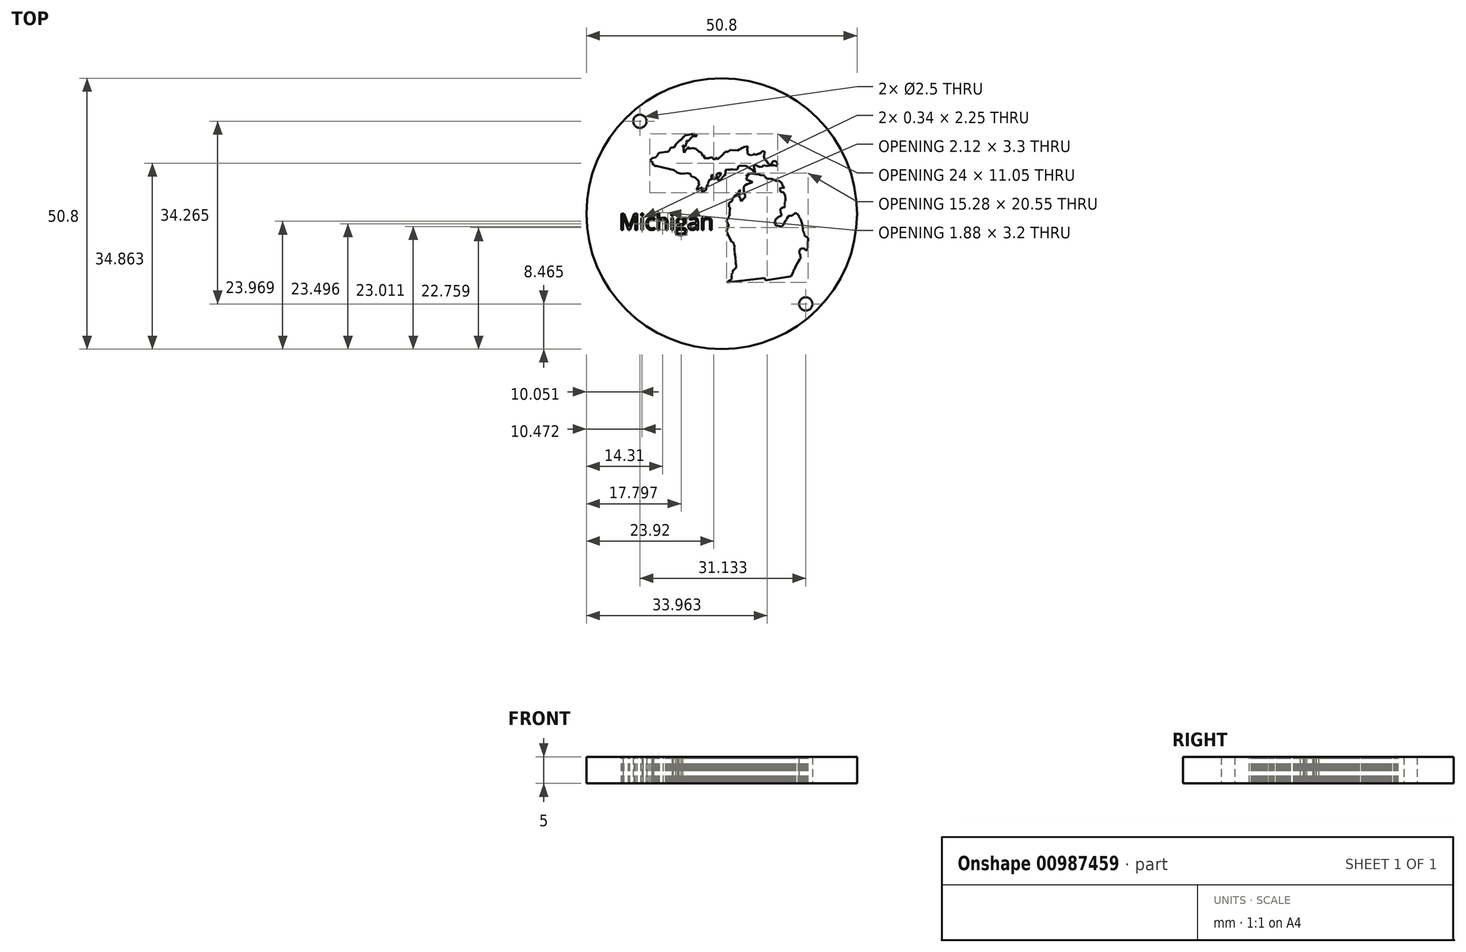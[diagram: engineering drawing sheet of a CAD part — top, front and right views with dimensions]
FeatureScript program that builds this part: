
annotation { "Feature Type Name" : "Feature", "Feature Type Description" : "" }
export const myFeature = defineFeature(function(context is Context, id is Id, definition is map)
    precondition{}
    {
        {
            var Q0;
            Q0=qCreatedBy(makeId("Top.planeOp"),FACE);
            var sketch = newSketch(context, id + "F0", { "sketchPlane" : qUnion([Q0])});
            skCircle(sketch, "E0", {"center": v(0, 0) * mm, "radius": 25.4 * mm});
            skCircle(sketch, "E1", {"center": v(-15.35, 17.33) * mm, "radius": 1.25 * mm});
            skCircle(sketch, "E2", {"center": v(15.78, -16.94) * mm, "radius": 1.25 * mm});
            skSolve(sketch);
        }
        {
            var Q0;
            Q0 = qSketchRegion(id + "F0", true);
            extrude(context, id + "F1", {"entities" : qUnion([Q0]), "depth" : 5 * mm, "offsetDistance" : 25 * mm});
        }
        {
            var Q0;
            Q0=makeQuery(id+"F1.opExtrude","CAP_FACE",FACE,{"disambiguationData":[OSD([sQuery(id+"F0.wireOp",EDGE,"E0"),sQuery(id+"F0.wireOp",EDGE,"E1"),sQuery(id+"F0.wireOp",EDGE,"E2")])],"isStart":false});
            var sketch = newSketch(context, id + "F2", { "sketchPlane" : qUnion([Q0])});
            skLineSegment(sketch, "E3", {"start": v(-7.31, 12.84) * mm, "end": v(-7.13, 12.4) * mm});
            skLineSegment(sketch, "E4", {"start": v(-7.13, 12.4) * mm, "end": v(-7.13, 11.84) * mm});
            skLineSegment(sketch, "E5", {"start": v(-7.13, 11.84) * mm, "end": v(-7.03, 11.43) * mm});
            skLineSegment(sketch, "E6", {"start": v(-7.03, 11.43) * mm, "end": v(-6.81, 11.86) * mm});
            skLineSegment(sketch, "E7", {"start": v(-6.81, 11.86) * mm, "end": v(-6.68, 12.01) * mm});
            skLineSegment(sketch, "E8", {"start": v(-6.68, 12.01) * mm, "end": v(-6.24, 12.44) * mm});
            skLineSegment(sketch, "E9", {"start": v(-6.24, 12.44) * mm, "end": v(-6.19, 12.44) * mm});
            skLineSegment(sketch, "E10", {"start": v(-6.19, 12.44) * mm, "end": v(-6.16, 12.37) * mm});
            skLineSegment(sketch, "E11", {"start": v(-6.16, 12.37) * mm, "end": v(-6.24, 12.27) * mm});
            skLineSegment(sketch, "E12", {"start": v(-6.24, 12.27) * mm, "end": v(-6.21, 12.17) * mm});
            skLineSegment(sketch, "E13", {"start": v(-6.21, 12.17) * mm, "end": v(-5.78, 12.22) * mm});
            skLineSegment(sketch, "E14", {"start": v(-5.78, 12.22) * mm, "end": v(-5.48, 12.33) * mm});
            skLineSegment(sketch, "E15", {"start": v(-5.48, 12.33) * mm, "end": v(-4.86, 12.2) * mm});
            skLineSegment(sketch, "E16", {"start": v(-4.86, 12.2) * mm, "end": v(-4.25, 11.64) * mm});
            skLineSegment(sketch, "E17", {"start": v(-4.25, 11.64) * mm, "end": v(-3.88, 11.5) * mm});
            skLineSegment(sketch, "E18", {"start": v(-3.88, 11.5) * mm, "end": v(-3.8, 11.41) * mm});
            skLineSegment(sketch, "E19", {"start": v(-3.8, 11.41) * mm, "end": v(-3.65, 11.04) * mm});
            skLineSegment(sketch, "E20", {"start": v(-3.65, 11.04) * mm, "end": v(-3.65, 10.97) * mm});
            skLineSegment(sketch, "E21", {"start": v(-3.65, 10.97) * mm, "end": v(-3.57, 10.86) * mm});
            skLineSegment(sketch, "E22", {"start": v(-3.57, 10.86) * mm, "end": v(-3.47, 10.86) * mm});
            skLineSegment(sketch, "E23", {"start": v(-3.47, 10.86) * mm, "end": v(-3.3, 10.9) * mm});
            skLineSegment(sketch, "E24", {"start": v(-3.3, 10.9) * mm, "end": v(-3.22, 10.82) * mm});
            skLineSegment(sketch, "E25", {"start": v(-3.22, 10.82) * mm, "end": v(-3.26, 10.58) * mm});
            skLineSegment(sketch, "E26", {"start": v(-3.26, 10.58) * mm, "end": v(-3.26, 10.44) * mm});
            skLineSegment(sketch, "E27", {"start": v(-3.26, 10.44) * mm, "end": v(-2.43, 10.44) * mm});
            skLineSegment(sketch, "E28", {"start": v(-2.43, 10.44) * mm, "end": v(-1.89, 10.61) * mm});
            skLineSegment(sketch, "E29", {"start": v(-1.89, 10.61) * mm, "end": v(-1.55, 10.3) * mm});
            skLineSegment(sketch, "E30", {"start": v(-1.55, 10.3) * mm, "end": v(-1.3, 10.16) * mm});
            skLineSegment(sketch, "E31", {"start": v(-1.3, 10.16) * mm, "end": v(-1.17, 10.31) * mm});
            skLineSegment(sketch, "E32", {"start": v(-1.17, 10.31) * mm, "end": v(-1.1, 10.45) * mm});
            skLineSegment(sketch, "E33", {"start": v(-1.1, 10.45) * mm, "end": v(-0.95, 10.45) * mm});
            skLineSegment(sketch, "E34", {"start": v(-0.95, 10.45) * mm, "end": v(-0.83, 10.26) * mm});
            skLineSegment(sketch, "E35", {"start": v(-0.83, 10.26) * mm, "end": v(-0.73, 10.21) * mm});
            skLineSegment(sketch, "E36", {"start": v(-0.73, 10.21) * mm, "end": v(0, 10.93) * mm});
            skLineSegment(sketch, "E37", {"start": v(0, 10.93) * mm, "end": v(0.07, 11) * mm});
            skLineSegment(sketch, "E38", {"start": v(0.07, 11) * mm, "end": v(0.15, 11.03) * mm});
            skLineSegment(sketch, "E39", {"start": v(0.15, 11.03) * mm, "end": v(0.18, 11.13) * mm});
            skLineSegment(sketch, "E40", {"start": v(0.18, 11.13) * mm, "end": v(0.34, 11.13) * mm});
            skLineSegment(sketch, "E41", {"start": v(0.34, 11.13) * mm, "end": v(0.37, 11.27) * mm});
            skLineSegment(sketch, "E42", {"start": v(0.37, 11.27) * mm, "end": v(0.71, 11.64) * mm});
            skLineSegment(sketch, "E43", {"start": v(0.71, 11.64) * mm, "end": v(1.16, 11.64) * mm});
            skLineSegment(sketch, "E44", {"start": v(1.16, 11.64) * mm, "end": v(1.6, 11.92) * mm});
            skLineSegment(sketch, "E45", {"start": v(1.6, 11.92) * mm, "end": v(1.74, 11.92) * mm});
            skLineSegment(sketch, "E46", {"start": v(1.74, 11.92) * mm, "end": v(1.8, 11.86) * mm});
            skLineSegment(sketch, "E47", {"start": v(1.8, 11.86) * mm, "end": v(1.84, 11.92) * mm});
            skLineSegment(sketch, "E48", {"start": v(1.84, 11.92) * mm, "end": v(3, 11.86) * mm});
            skLineSegment(sketch, "E49", {"start": v(3, 11.86) * mm, "end": v(3.33, 12.08) * mm});
            skLineSegment(sketch, "E50", {"start": v(3.33, 12.08) * mm, "end": v(3.46, 12.08) * mm});
            skLineSegment(sketch, "E51", {"start": v(3.46, 12.08) * mm, "end": v(3.53, 12.02) * mm});
            skLineSegment(sketch, "E52", {"start": v(3.53, 12.02) * mm, "end": v(3.58, 12.26) * mm});
            skLineSegment(sketch, "E53", {"start": v(3.58, 12.26) * mm, "end": v(3.69, 12.3) * mm});
            skLineSegment(sketch, "E54", {"start": v(3.69, 12.3) * mm, "end": v(3.77, 12.21) * mm});
            skLineSegment(sketch, "E55", {"start": v(3.77, 12.21) * mm, "end": v(3.78, 12.33) * mm});
            skLineSegment(sketch, "E56", {"start": v(3.78, 12.33) * mm, "end": v(3.9, 12.37) * mm});
            skLineSegment(sketch, "E57", {"start": v(3.9, 12.37) * mm, "end": v(4.04, 12.26) * mm});
            skLineSegment(sketch, "E58", {"start": v(4.04, 12.26) * mm, "end": v(4.05, 12.48) * mm});
            skLineSegment(sketch, "E59", {"start": v(4.05, 12.48) * mm, "end": v(4.9, 12.65) * mm});
            skLineSegment(sketch, "E60", {"start": v(4.9, 12.65) * mm, "end": v(4.79, 12.11) * mm});
            skLineSegment(sketch, "E61", {"start": v(4.79, 12.11) * mm, "end": v(4.79, 11.92) * mm});
            skLineSegment(sketch, "E62", {"start": v(4.79, 11.92) * mm, "end": v(4.83, 11.77) * mm});
            skLineSegment(sketch, "E63", {"start": v(4.83, 11.77) * mm, "end": v(4.83, 11.43) * mm});
            skLineSegment(sketch, "E64", {"start": v(4.83, 11.43) * mm, "end": v(4.82, 11.27) * mm});
            skLineSegment(sketch, "E65", {"start": v(4.82, 11.27) * mm, "end": v(4.92, 11.23) * mm});
            skLineSegment(sketch, "E66", {"start": v(4.92, 11.23) * mm, "end": v(5.06, 11.13) * mm});
            skLineSegment(sketch, "E67", {"start": v(5.06, 11.13) * mm, "end": v(5.09, 11.04) * mm});
            skLineSegment(sketch, "E68", {"start": v(5.09, 11.04) * mm, "end": v(5.26, 11.04) * mm});
            skLineSegment(sketch, "E69", {"start": v(5.26, 11.04) * mm, "end": v(5.36, 11) * mm});
            skLineSegment(sketch, "E70", {"start": v(5.36, 11) * mm, "end": v(5.4, 10.9) * mm});
            skLineSegment(sketch, "E71", {"start": v(5.4, 10.9) * mm, "end": v(5.6, 11.04) * mm});
            skLineSegment(sketch, "E72", {"start": v(5.6, 11.04) * mm, "end": v(5.81, 10.95) * mm});
            skLineSegment(sketch, "E73", {"start": v(5.81, 10.95) * mm, "end": v(5.9, 11.16) * mm});
            skLineSegment(sketch, "E74", {"start": v(5.9, 11.16) * mm, "end": v(6.03, 11.2) * mm});
            skLineSegment(sketch, "E75", {"start": v(6.03, 11.2) * mm, "end": v(6.36, 11.04) * mm});
            skLineSegment(sketch, "E76", {"start": v(6.36, 11.04) * mm, "end": v(6.9, 11.22) * mm});
            skLineSegment(sketch, "E77", {"start": v(6.9, 11.22) * mm, "end": v(7.07, 11.22) * mm});
            skLineSegment(sketch, "E78", {"start": v(7.07, 11.22) * mm, "end": v(7.27, 11.43) * mm});
            skLineSegment(sketch, "E79", {"start": v(7.27, 11.43) * mm, "end": v(7.33, 11.38) * mm});
            skLineSegment(sketch, "E80", {"start": v(7.33, 11.38) * mm, "end": v(7.41, 11.34) * mm});
            skLineSegment(sketch, "E81", {"start": v(7.41, 11.34) * mm, "end": v(7.37, 11.48) * mm});
            skLineSegment(sketch, "E82", {"start": v(7.37, 11.48) * mm, "end": v(7.42, 11.54) * mm});
            skLineSegment(sketch, "E83", {"start": v(7.42, 11.54) * mm, "end": v(7.5, 11.46) * mm});
            skLineSegment(sketch, "E84", {"start": v(7.5, 11.46) * mm, "end": v(7.5, 11.67) * mm});
            skLineSegment(sketch, "E85", {"start": v(7.5, 11.67) * mm, "end": v(7.96, 11.75) * mm});
            skLineSegment(sketch, "E86", {"start": v(7.96, 11.75) * mm, "end": v(8.08, 11.27) * mm});
            skLineSegment(sketch, "E87", {"start": v(8.08, 11.27) * mm, "end": v(7.92, 10.9) * mm});
            skLineSegment(sketch, "E88", {"start": v(7.92, 10.9) * mm, "end": v(7.95, 10.75) * mm});
            skLineSegment(sketch, "E89", {"start": v(7.95, 10.75) * mm, "end": v(7.99, 10.5) * mm});
            skLineSegment(sketch, "E90", {"start": v(7.99, 10.5) * mm, "end": v(8.02, 10.29) * mm});
            skLineSegment(sketch, "E91", {"start": v(8.02, 10.29) * mm, "end": v(8.1, 10.21) * mm});
            skLineSegment(sketch, "E92", {"start": v(8.1, 10.21) * mm, "end": v(8.15, 10.06) * mm});
            skLineSegment(sketch, "E93", {"start": v(8.15, 10.06) * mm, "end": v(8.47, 9.89) * mm});
            skLineSegment(sketch, "E94", {"start": v(8.47, 9.89) * mm, "end": v(8.72, 9.3) * mm});
            skLineSegment(sketch, "E95", {"start": v(8.72, 9.3) * mm, "end": v(8.86, 9.3) * mm});
            skLineSegment(sketch, "E96", {"start": v(8.86, 9.3) * mm, "end": v(9.03, 9.2) * mm});
            skLineSegment(sketch, "E97", {"start": v(9.03, 9.2) * mm, "end": v(9.46, 9.43) * mm});
            skLineSegment(sketch, "E98", {"start": v(9.46, 9.43) * mm, "end": v(9.58, 9.57) * mm});
            skLineSegment(sketch, "E99", {"start": v(9.58, 9.57) * mm, "end": v(9.55, 9.8) * mm});
            skLineSegment(sketch, "E100", {"start": v(9.55, 9.8) * mm, "end": v(10.07, 9.9) * mm});
            skLineSegment(sketch, "E101", {"start": v(10.07, 9.9) * mm, "end": v(10.52, 9.47) * mm});
            skLineSegment(sketch, "E102", {"start": v(10.52, 9.47) * mm, "end": v(10.3, 8.97) * mm});
            skLineSegment(sketch, "E103", {"start": v(10.3, 8.97) * mm, "end": v(10.19, 8.93) * mm});
            skLineSegment(sketch, "E104", {"start": v(10.19, 8.93) * mm, "end": v(10.02, 9.1) * mm});
            skLineSegment(sketch, "E105", {"start": v(10.02, 9.1) * mm, "end": v(9.76, 9.1) * mm});
            skLineSegment(sketch, "E106", {"start": v(9.76, 9.1) * mm, "end": v(9.41, 9.05) * mm});
            skLineSegment(sketch, "E107", {"start": v(9.41, 9.05) * mm, "end": v(8.55, 8.96) * mm});
            skLineSegment(sketch, "E108", {"start": v(8.55, 8.96) * mm, "end": v(7.86, 9.06) * mm});
            skLineSegment(sketch, "E109", {"start": v(7.86, 9.06) * mm, "end": v(7.66, 8.85) * mm});
            skLineSegment(sketch, "E110", {"start": v(7.66, 8.85) * mm, "end": v(7.13, 8.73) * mm});
            skLineSegment(sketch, "E111", {"start": v(7.13, 8.73) * mm, "end": v(6.73, 8.94) * mm});
            skLineSegment(sketch, "E112", {"start": v(6.73, 8.94) * mm, "end": v(6.59, 9.07) * mm});
            skLineSegment(sketch, "E113", {"start": v(6.59, 9.07) * mm, "end": v(6.47, 9.1) * mm});
            skLineSegment(sketch, "E114", {"start": v(6.47, 9.1) * mm, "end": v(6.3, 9.11) * mm});
            skLineSegment(sketch, "E115", {"start": v(6.3, 9.11) * mm, "end": v(6.1, 9.08) * mm});
            skLineSegment(sketch, "E116", {"start": v(6.1, 9.08) * mm, "end": v(6.03, 8.95) * mm});
            skLineSegment(sketch, "E117", {"start": v(6.03, 8.95) * mm, "end": v(6.03, 8.68) * mm});
            skLineSegment(sketch, "E118", {"start": v(6.03, 8.68) * mm, "end": v(6.1, 8.49) * mm});
            skLineSegment(sketch, "E119", {"start": v(6.1, 8.49) * mm, "end": v(6.17, 8.26) * mm});
            skLineSegment(sketch, "E120", {"start": v(6.17, 8.26) * mm, "end": v(6.25, 7.79) * mm});
            skLineSegment(sketch, "E121", {"start": v(6.25, 7.79) * mm, "end": v(6.25, 7.64) * mm});
            skLineSegment(sketch, "E122", {"start": v(6.25, 7.64) * mm, "end": v(6.2, 7.64) * mm});
            skLineSegment(sketch, "E123", {"start": v(6.2, 7.64) * mm, "end": v(5.74, 8.23) * mm});
            skLineSegment(sketch, "E124", {"start": v(5.74, 8.23) * mm, "end": v(5.19, 8.59) * mm});
            skLineSegment(sketch, "E125", {"start": v(5.19, 8.59) * mm, "end": v(5.04, 8.63) * mm});
            skLineSegment(sketch, "E126", {"start": v(5.04, 8.63) * mm, "end": v(4.9, 8.75) * mm});
            skLineSegment(sketch, "E127", {"start": v(4.9, 8.75) * mm, "end": v(4.67, 8.86) * mm});
            skLineSegment(sketch, "E128", {"start": v(4.67, 8.86) * mm, "end": v(4.55, 8.97) * mm});
            skLineSegment(sketch, "E129", {"start": v(4.55, 8.97) * mm, "end": v(3.33, 9.03) * mm});
            skLineSegment(sketch, "E130", {"start": v(3.33, 9.03) * mm, "end": v(3.24, 8.87) * mm});
            skLineSegment(sketch, "E131", {"start": v(3.24, 8.87) * mm, "end": v(3.1, 8.87) * mm});
            skLineSegment(sketch, "E132", {"start": v(3.1, 8.87) * mm, "end": v(3.1, 8.67) * mm});
            skLineSegment(sketch, "E133", {"start": v(3.1, 8.67) * mm, "end": v(3, 8.45) * mm});
            skLineSegment(sketch, "E134", {"start": v(3, 8.45) * mm, "end": v(2.85, 8.26) * mm});
            skLineSegment(sketch, "E135", {"start": v(2.85, 8.26) * mm, "end": v(2.6, 8.27) * mm});
            skLineSegment(sketch, "E136", {"start": v(2.6, 8.27) * mm, "end": v(1.93, 8.3) * mm});
            skLineSegment(sketch, "E137", {"start": v(1.93, 8.3) * mm, "end": v(1.8, 8.35) * mm});
            skLineSegment(sketch, "E138", {"start": v(1.8, 8.35) * mm, "end": v(1.7, 8.25) * mm});
            skLineSegment(sketch, "E139", {"start": v(1.7, 8.25) * mm, "end": v(1.24, 8.27) * mm});
            skLineSegment(sketch, "E140", {"start": v(1.24, 8.27) * mm, "end": v(1.07, 8.37) * mm});
            skLineSegment(sketch, "E141", {"start": v(1.07, 8.37) * mm, "end": v(1, 8.27) * mm});
            skLineSegment(sketch, "E142", {"start": v(1, 8.27) * mm, "end": v(0.71, 8.17) * mm});
            skLineSegment(sketch, "E143", {"start": v(0.71, 8.17) * mm, "end": v(0.71, 7.97) * mm});
            skLineSegment(sketch, "E144", {"start": v(0.71, 7.97) * mm, "end": v(0.71, 7.48) * mm});
            skLineSegment(sketch, "E145", {"start": v(0.71, 7.48) * mm, "end": v(0.62, 7.3) * mm});
            skLineSegment(sketch, "E146", {"start": v(0.62, 7.3) * mm, "end": v(0.54, 7.15) * mm});
            skLineSegment(sketch, "E147", {"start": v(0.54, 7.15) * mm, "end": v(0.41, 7.1) * mm});
            skLineSegment(sketch, "E148", {"start": v(0.41, 7.1) * mm, "end": v(0.35, 7) * mm});
            skLineSegment(sketch, "E149", {"start": v(0.35, 7) * mm, "end": v(0.25, 6.96) * mm});
            skLineSegment(sketch, "E150", {"start": v(0.25, 6.96) * mm, "end": v(0.25, 6.86) * mm});
            skLineSegment(sketch, "E151", {"start": v(0.25, 6.86) * mm, "end": v(0.18, 6.87) * mm});
            skLineSegment(sketch, "E152", {"start": v(0.18, 6.87) * mm, "end": v(0.18, 6.77) * mm});
            skLineSegment(sketch, "E153", {"start": v(0.18, 6.77) * mm, "end": v(-0.2, 6.37) * mm});
            skLineSegment(sketch, "E154", {"start": v(-0.2, 6.37) * mm, "end": v(-0.65, 6.22) * mm});
            skLineSegment(sketch, "E155", {"start": v(-0.65, 6.22) * mm, "end": v(-0.76, 6.56) * mm});
            skLineSegment(sketch, "E156", {"start": v(-0.76, 6.56) * mm, "end": v(-0.52, 6.95) * mm});
            skLineSegment(sketch, "E157", {"start": v(-0.52, 6.95) * mm, "end": v(-0.43, 6.95) * mm});
            skLineSegment(sketch, "E158", {"start": v(-0.43, 6.95) * mm, "end": v(-0.45, 7.04) * mm});
            skLineSegment(sketch, "E159", {"start": v(-0.45, 7.04) * mm, "end": v(-0.3, 7.13) * mm});
            skLineSegment(sketch, "E160", {"start": v(-0.3, 7.13) * mm, "end": v(-0.2, 7.23) * mm});
            skLineSegment(sketch, "E161", {"start": v(-0.2, 7.23) * mm, "end": v(-0.15, 7.48) * mm});
            skLineSegment(sketch, "E162", {"start": v(-0.15, 7.48) * mm, "end": v(-0.18, 7.63) * mm});
            skLineSegment(sketch, "E163", {"start": v(-0.18, 7.63) * mm, "end": v(-0.24, 7.67) * mm});
            skLineSegment(sketch, "E164", {"start": v(-0.24, 7.67) * mm, "end": v(-0.5, 7.59) * mm});
            skLineSegment(sketch, "E165", {"start": v(-0.5, 7.59) * mm, "end": v(-0.57, 7.59) * mm});
            skLineSegment(sketch, "E166", {"start": v(-0.57, 7.59) * mm, "end": v(-0.57, 7.53) * mm});
            skLineSegment(sketch, "E167", {"start": v(-0.57, 7.53) * mm, "end": v(-0.75, 7.53) * mm});
            skLineSegment(sketch, "E168", {"start": v(-0.75, 7.53) * mm, "end": v(-0.8, 7.56) * mm});
            skLineSegment(sketch, "E169", {"start": v(-0.8, 7.56) * mm, "end": v(-0.78, 7.47) * mm});
            skLineSegment(sketch, "E170", {"start": v(-0.78, 7.47) * mm, "end": v(-0.93, 7.45) * mm});
            skLineSegment(sketch, "E171", {"start": v(-0.93, 7.45) * mm, "end": v(-1, 7.45) * mm});
            skLineSegment(sketch, "E172", {"start": v(-1, 7.45) * mm, "end": v(-0.98, 7.3) * mm});
            skLineSegment(sketch, "E173", {"start": v(-0.98, 7.3) * mm, "end": v(-0.96, 7.22) * mm});
            skLineSegment(sketch, "E174", {"start": v(-0.96, 7.22) * mm, "end": v(-0.98, 6.64) * mm});
            skLineSegment(sketch, "E175", {"start": v(-0.98, 6.64) * mm, "end": v(-1.48, 6.48) * mm});
            skLineSegment(sketch, "E176", {"start": v(-1.48, 6.48) * mm, "end": v(-1.56, 6.48) * mm});
            skLineSegment(sketch, "E177", {"start": v(-1.56, 6.48) * mm, "end": v(-1.56, 6.68) * mm});
            skLineSegment(sketch, "E178", {"start": v(-1.56, 6.68) * mm, "end": v(-1.58, 6.75) * mm});
            skLineSegment(sketch, "E179", {"start": v(-1.58, 6.75) * mm, "end": v(-1.46, 6.79) * mm});
            skLineSegment(sketch, "E180", {"start": v(-1.46, 6.79) * mm, "end": v(-1.59, 6.95) * mm});
            skLineSegment(sketch, "E181", {"start": v(-1.59, 6.95) * mm, "end": v(-1.58, 7.09) * mm});
            skLineSegment(sketch, "E182", {"start": v(-1.58, 7.09) * mm, "end": v(-1.7, 7.15) * mm});
            skLineSegment(sketch, "E183", {"start": v(-1.7, 7.15) * mm, "end": v(-1.8, 7.33) * mm});
            skLineSegment(sketch, "E184", {"start": v(-1.8, 7.33) * mm, "end": v(-1.88, 7.17) * mm});
            skLineSegment(sketch, "E185", {"start": v(-1.88, 7.17) * mm, "end": v(-1.87, 7.12) * mm});
            skLineSegment(sketch, "E186", {"start": v(-1.87, 7.12) * mm, "end": v(-1.94, 7.13) * mm});
            skLineSegment(sketch, "E187", {"start": v(-1.94, 7.13) * mm, "end": v(-1.95, 6.96) * mm});
            skLineSegment(sketch, "E188", {"start": v(-1.95, 6.96) * mm, "end": v(-1.95, 6.85) * mm});
            skLineSegment(sketch, "E189", {"start": v(-1.95, 6.85) * mm, "end": v(-1.9, 6.71) * mm});
            skLineSegment(sketch, "E190", {"start": v(-1.9, 6.71) * mm, "end": v(-1.77, 6.51) * mm});
            skLineSegment(sketch, "E191", {"start": v(-1.77, 6.51) * mm, "end": v(-1.83, 6.44) * mm});
            skLineSegment(sketch, "E192", {"start": v(-1.83, 6.44) * mm, "end": v(-1.94, 6.5) * mm});
            skLineSegment(sketch, "E193", {"start": v(-1.94, 6.5) * mm, "end": v(-2.06, 6.46) * mm});
            skLineSegment(sketch, "E194", {"start": v(-2.06, 6.46) * mm, "end": v(-2.2, 6.46) * mm});
            skLineSegment(sketch, "E195", {"start": v(-2.2, 6.46) * mm, "end": v(-2.3, 6.28) * mm});
            skLineSegment(sketch, "E196", {"start": v(-2.3, 6.28) * mm, "end": v(-2.42, 6.04) * mm});
            skLineSegment(sketch, "E197", {"start": v(-2.42, 6.04) * mm, "end": v(-2.52, 5.93) * mm});
            skLineSegment(sketch, "E198", {"start": v(-2.52, 5.93) * mm, "end": v(-2.52, 5.74) * mm});
            skLineSegment(sketch, "E199", {"start": v(-2.52, 5.74) * mm, "end": v(-2.63, 5.63) * mm});
            skLineSegment(sketch, "E200", {"start": v(-2.63, 5.63) * mm, "end": v(-2.6, 5.49) * mm});
            skLineSegment(sketch, "E201", {"start": v(-2.6, 5.49) * mm, "end": v(-2.81, 5.07) * mm});
            skLineSegment(sketch, "E202", {"start": v(-2.81, 5.07) * mm, "end": v(-2.91, 4.68) * mm});
            skLineSegment(sketch, "E203", {"start": v(-2.91, 4.68) * mm, "end": v(-2.97, 4.45) * mm});
            skLineSegment(sketch, "E204", {"start": v(-2.97, 4.45) * mm, "end": v(-3.01, 4.36) * mm});
            skLineSegment(sketch, "E205", {"start": v(-3.01, 4.36) * mm, "end": v(-3.08, 4.44) * mm});
            skLineSegment(sketch, "E206", {"start": v(-3.08, 4.44) * mm, "end": v(-3.12, 4.3) * mm});
            skLineSegment(sketch, "E207", {"start": v(-3.12, 4.3) * mm, "end": v(-3.65, 3.94) * mm});
            skLineSegment(sketch, "E208", {"start": v(-3.65, 3.94) * mm, "end": v(-3.74, 4) * mm});
            skLineSegment(sketch, "E209", {"start": v(-3.74, 4) * mm, "end": v(-3.74, 4.21) * mm});
            skLineSegment(sketch, "E210", {"start": v(-3.74, 4.21) * mm, "end": v(-3.5, 4.48) * mm});
            skLineSegment(sketch, "E211", {"start": v(-3.5, 4.48) * mm, "end": v(-3.62, 4.5) * mm});
            skLineSegment(sketch, "E212", {"start": v(-3.62, 4.5) * mm, "end": v(-3.68, 4.57) * mm});
            skLineSegment(sketch, "E213", {"start": v(-3.68, 4.57) * mm, "end": v(-3.59, 4.76) * mm});
            skLineSegment(sketch, "E214", {"start": v(-3.59, 4.76) * mm, "end": v(-3.65, 4.89) * mm});
            skLineSegment(sketch, "E215", {"start": v(-3.65, 4.89) * mm, "end": v(-3.74, 4.88) * mm});
            skLineSegment(sketch, "E216", {"start": v(-3.74, 4.88) * mm, "end": v(-3.94, 4.74) * mm});
            skLineSegment(sketch, "E217", {"start": v(-3.94, 4.74) * mm, "end": v(-4.16, 4.84) * mm});
            skLineSegment(sketch, "E218", {"start": v(-4.16, 4.84) * mm, "end": v(-4.25, 4.65) * mm});
            skLineSegment(sketch, "E219", {"start": v(-4.25, 4.65) * mm, "end": v(-4.36, 4.6) * mm});
            skLineSegment(sketch, "E220", {"start": v(-4.36, 4.6) * mm, "end": v(-4.5, 4.6) * mm});
            skLineSegment(sketch, "E221", {"start": v(-4.5, 4.6) * mm, "end": v(-4.6, 4.48) * mm});
            skLineSegment(sketch, "E222", {"start": v(-4.6, 4.48) * mm, "end": v(-4.72, 4.48) * mm});
            skLineSegment(sketch, "E223", {"start": v(-4.72, 4.48) * mm, "end": v(-4.68, 4.65) * mm});
            skLineSegment(sketch, "E224", {"start": v(-4.68, 4.65) * mm, "end": v(-4.18, 5.66) * mm});
            skLineSegment(sketch, "E225", {"start": v(-4.18, 5.66) * mm, "end": v(-4.32, 5.66) * mm});
            skLineSegment(sketch, "E226", {"start": v(-4.32, 5.66) * mm, "end": v(-4.35, 5.74) * mm});
            skLineSegment(sketch, "E227", {"start": v(-4.35, 5.74) * mm, "end": v(-4.16, 5.88) * mm});
            skLineSegment(sketch, "E228", {"start": v(-4.16, 5.88) * mm, "end": v(-4.38, 6) * mm});
            skLineSegment(sketch, "E229", {"start": v(-4.38, 6) * mm, "end": v(-4.4, 6.04) * mm});
            skLineSegment(sketch, "E230", {"start": v(-4.4, 6.04) * mm, "end": v(-4.28, 6.09) * mm});
            skLineSegment(sketch, "E231", {"start": v(-4.28, 6.09) * mm, "end": v(-5, 6.8) * mm});
            skLineSegment(sketch, "E232", {"start": v(-5, 6.8) * mm, "end": v(-5.13, 6.8) * mm});
            skLineSegment(sketch, "E233", {"start": v(-5.13, 6.8) * mm, "end": v(-5.26, 6.9) * mm});
            skLineSegment(sketch, "E234", {"start": v(-5.26, 6.9) * mm, "end": v(-5.51, 6.86) * mm});
            skLineSegment(sketch, "E235", {"start": v(-5.51, 6.86) * mm, "end": v(-5.6, 7.02) * mm});
            skLineSegment(sketch, "E236", {"start": v(-5.6, 7.02) * mm, "end": v(-5.7, 6.96) * mm});
            skLineSegment(sketch, "E237", {"start": v(-5.7, 6.96) * mm, "end": v(-5.74, 7.05) * mm});
            skLineSegment(sketch, "E238", {"start": v(-5.74, 7.05) * mm, "end": v(-5.68, 7.16) * mm});
            skLineSegment(sketch, "E239", {"start": v(-5.68, 7.16) * mm, "end": v(-5.9, 7.23) * mm});
            skLineSegment(sketch, "E240", {"start": v(-5.9, 7.23) * mm, "end": v(-5.88, 7.49) * mm});
            skLineSegment(sketch, "E241", {"start": v(-5.88, 7.49) * mm, "end": v(-6.56, 7.6) * mm});
            skLineSegment(sketch, "E242", {"start": v(-6.56, 7.6) * mm, "end": v(-6.74, 7.48) * mm});
            skLineSegment(sketch, "E243", {"start": v(-6.74, 7.48) * mm, "end": v(-6.88, 7.59) * mm});
            skLineSegment(sketch, "E244", {"start": v(-6.88, 7.59) * mm, "end": v(-6.98, 7.53) * mm});
            skLineSegment(sketch, "E245", {"start": v(-6.98, 7.53) * mm, "end": v(-7.11, 7.58) * mm});
            skLineSegment(sketch, "E246", {"start": v(-7.11, 7.58) * mm, "end": v(-7.5, 7.52) * mm});
            skLineSegment(sketch, "E247", {"start": v(-7.5, 7.52) * mm, "end": v(-8.26, 7.7) * mm});
            skLineSegment(sketch, "E248", {"start": v(-8.26, 7.7) * mm, "end": v(-9, 8.18) * mm});
            skLineSegment(sketch, "E249", {"start": v(-9, 8.18) * mm, "end": v(-12.25, 8.94) * mm});
            skLineSegment(sketch, "E250", {"start": v(-12.25, 8.94) * mm, "end": v(-12.42, 8.92) * mm});
            skLineSegment(sketch, "E251", {"start": v(-12.42, 8.92) * mm, "end": v(-12.6, 8.92) * mm});
            skLineSegment(sketch, "E252", {"start": v(-12.6, 8.92) * mm, "end": v(-12.63, 9.06) * mm});
            skLineSegment(sketch, "E253", {"start": v(-12.63, 9.06) * mm, "end": v(-12.73, 9.01) * mm});
            skLineSegment(sketch, "E254", {"start": v(-12.73, 9.01) * mm, "end": v(-12.76, 9.2) * mm});
            skLineSegment(sketch, "E255", {"start": v(-12.76, 9.2) * mm, "end": v(-12.79, 9.33) * mm});
            skLineSegment(sketch, "E256", {"start": v(-12.79, 9.33) * mm, "end": v(-13.03, 9.32) * mm});
            skLineSegment(sketch, "E257", {"start": v(-13.03, 9.32) * mm, "end": v(-13.03, 9.38) * mm});
            skLineSegment(sketch, "E258", {"start": v(-13.03, 9.38) * mm, "end": v(-12.86, 9.57) * mm});
            skLineSegment(sketch, "E259", {"start": v(-12.86, 9.57) * mm, "end": v(-12.94, 9.62) * mm});
            skLineSegment(sketch, "E260", {"start": v(-12.94, 9.62) * mm, "end": v(-13.11, 9.63) * mm});
            skLineSegment(sketch, "E261", {"start": v(-13.11, 9.63) * mm, "end": v(-13.15, 9.75) * mm});
            skLineSegment(sketch, "E262", {"start": v(-13.15, 9.75) * mm, "end": v(-13.48, 9.96) * mm});
            skLineSegment(sketch, "E263", {"start": v(-13.48, 9.96) * mm, "end": v(-13.07, 10.4) * mm});
            skLineSegment(sketch, "E264", {"start": v(-13.07, 10.4) * mm, "end": v(-12.9, 10.4) * mm});
            skLineSegment(sketch, "E265", {"start": v(-12.9, 10.4) * mm, "end": v(-12.78, 10.52) * mm});
            skLineSegment(sketch, "E266", {"start": v(-12.78, 10.52) * mm, "end": v(-12.53, 10.46) * mm});
            skLineSegment(sketch, "E267", {"start": v(-12.53, 10.46) * mm, "end": v(-12.38, 10.63) * mm});
            skLineSegment(sketch, "E268", {"start": v(-12.38, 10.63) * mm, "end": v(-12.3, 10.62) * mm});
            skLineSegment(sketch, "E269", {"start": v(-12.3, 10.62) * mm, "end": v(-12.27, 10.78) * mm});
            skLineSegment(sketch, "E270", {"start": v(-12.27, 10.78) * mm, "end": v(-12.09, 10.77) * mm});
            skLineSegment(sketch, "E271", {"start": v(-12.09, 10.77) * mm, "end": v(-12.13, 10.9) * mm});
            skLineSegment(sketch, "E272", {"start": v(-12.13, 10.9) * mm, "end": v(-12.06, 11.01) * mm});
            skLineSegment(sketch, "E273", {"start": v(-12.06, 11.01) * mm, "end": v(-11.96, 11) * mm});
            skLineSegment(sketch, "E274", {"start": v(-11.96, 11) * mm, "end": v(-12.01, 11.13) * mm});
            skLineSegment(sketch, "E275", {"start": v(-12.01, 11.13) * mm, "end": v(-11.75, 11.4) * mm});
            skLineSegment(sketch, "E276", {"start": v(-11.75, 11.4) * mm, "end": v(-10.28, 11.64) * mm});
            skLineSegment(sketch, "E277", {"start": v(-10.28, 11.64) * mm, "end": v(-10.1, 11.62) * mm});
            skLineSegment(sketch, "E278", {"start": v(-10.1, 11.62) * mm, "end": v(-9.9, 11.75) * mm});
            skLineSegment(sketch, "E279", {"start": v(-9.9, 11.75) * mm, "end": v(-9.86, 11.87) * mm});
            skLineSegment(sketch, "E280", {"start": v(-9.86, 11.87) * mm, "end": v(-9.75, 11.92) * mm});
            skLineSegment(sketch, "E281", {"start": v(-9.75, 11.92) * mm, "end": v(-9.74, 12.1) * mm});
            skLineSegment(sketch, "E282", {"start": v(-9.74, 12.1) * mm, "end": v(-9.63, 12.2) * mm});
            skLineSegment(sketch, "E283", {"start": v(-9.63, 12.2) * mm, "end": v(-9.57, 12.4) * mm});
            skLineSegment(sketch, "E284", {"start": v(-9.57, 12.4) * mm, "end": v(-9.3, 12.38) * mm});
            skLineSegment(sketch, "E285", {"start": v(-9.3, 12.38) * mm, "end": v(-9.1, 12.46) * mm});
            skLineSegment(sketch, "E286", {"start": v(-9.1, 12.46) * mm, "end": v(-8.92, 12.45) * mm});
            skLineSegment(sketch, "E287", {"start": v(-8.92, 12.45) * mm, "end": v(-8.8, 12.55) * mm});
            skLineSegment(sketch, "E288", {"start": v(-8.8, 12.55) * mm, "end": v(-8.65, 12.94) * mm});
            skLineSegment(sketch, "E289", {"start": v(-8.65, 12.94) * mm, "end": v(-8.14, 13.48) * mm});
            skLineSegment(sketch, "E290", {"start": v(-8.14, 13.48) * mm, "end": v(-8.1, 13.58) * mm});
            skLineSegment(sketch, "E291", {"start": v(-8.1, 13.58) * mm, "end": v(-7.63, 13.83) * mm});
            skLineSegment(sketch, "E292", {"start": v(-7.63, 13.83) * mm, "end": v(-7.03, 14.54) * mm});
            skLineSegment(sketch, "E293", {"start": v(-7.03, 14.54) * mm, "end": v(-6.97, 14.66) * mm});
            skLineSegment(sketch, "E294", {"start": v(-6.97, 14.66) * mm, "end": v(-6.78, 14.72) * mm});
            skLineSegment(sketch, "E295", {"start": v(-6.78, 14.72) * mm, "end": v(-6.73, 14.67) * mm});
            skLineSegment(sketch, "E296", {"start": v(-6.73, 14.67) * mm, "end": v(-6.64, 14.74) * mm});
            skLineSegment(sketch, "E297", {"start": v(-6.64, 14.74) * mm, "end": v(-5.3, 14.95) * mm});
            skLineSegment(sketch, "E298", {"start": v(-5.3, 14.95) * mm, "end": v(-5.08, 14.92) * mm});
            skLineSegment(sketch, "E299", {"start": v(-5.08, 14.92) * mm, "end": v(-5.07, 14.83) * mm});
            skLineSegment(sketch, "E300", {"start": v(-5.07, 14.83) * mm, "end": v(-5, 14.95) * mm});
            skLineSegment(sketch, "E301", {"start": v(-5, 14.95) * mm, "end": v(-4.95, 14.8) * mm});
            skLineSegment(sketch, "E302", {"start": v(-4.95, 14.8) * mm, "end": v(-4.86, 14.99) * mm});
            skLineSegment(sketch, "E303", {"start": v(-4.86, 14.99) * mm, "end": v(-4.66, 14.54) * mm});
            skLineSegment(sketch, "E304", {"start": v(-4.66, 14.54) * mm, "end": v(-4.89, 14.52) * mm});
            skLineSegment(sketch, "E305", {"start": v(-4.89, 14.52) * mm, "end": v(-4.98, 14.6) * mm});
            skLineSegment(sketch, "E306", {"start": v(-4.98, 14.6) * mm, "end": v(-5.04, 14.53) * mm});
            skLineSegment(sketch, "E307", {"start": v(-5.04, 14.53) * mm, "end": v(-5.6, 14.52) * mm});
            skLineSegment(sketch, "E308", {"start": v(-5.6, 14.52) * mm, "end": v(-5.57, 14.33) * mm});
            skLineSegment(sketch, "E309", {"start": v(-5.57, 14.33) * mm, "end": v(-5.8, 14.18) * mm});
            skLineSegment(sketch, "E310", {"start": v(-5.8, 14.18) * mm, "end": v(-6.16, 13.8) * mm});
            skLineSegment(sketch, "E311", {"start": v(-6.16, 13.8) * mm, "end": v(-6.36, 13.61) * mm});
            skLineSegment(sketch, "E312", {"start": v(-6.36, 13.61) * mm, "end": v(-6.62, 13.7) * mm});
            skLineSegment(sketch, "E313", {"start": v(-6.62, 13.7) * mm, "end": v(-6.51, 13.35) * mm});
            skLineSegment(sketch, "E314", {"start": v(-6.51, 13.35) * mm, "end": v(-6.57, 13.25) * mm});
            skLineSegment(sketch, "E315", {"start": v(-6.57, 13.25) * mm, "end": v(-6.59, 13.15) * mm});
            skLineSegment(sketch, "E316", {"start": v(-6.59, 13.15) * mm, "end": v(-6.84, 13.07) * mm});
            skLineSegment(sketch, "E317", {"start": v(-6.84, 13.07) * mm, "end": v(-6.7, 12.92) * mm});
            skLineSegment(sketch, "E318", {"start": v(-6.7, 12.92) * mm, "end": v(-6.8, 12.6) * mm});
            skLineSegment(sketch, "E319", {"start": v(-6.8, 12.6) * mm, "end": v(-7.31, 12.84) * mm});
            skLineSegment(sketch, "E320", {"start": v(5.6, 7.54) * mm, "end": v(6.03, 7.54) * mm});
            skLineSegment(sketch, "E321", {"start": v(6.03, 7.54) * mm, "end": v(6.08, 7.41) * mm});
            skLineSegment(sketch, "E322", {"start": v(6.08, 7.41) * mm, "end": v(6.3, 7.55) * mm});
            skLineSegment(sketch, "E323", {"start": v(6.3, 7.55) * mm, "end": v(6.36, 7.3) * mm});
            skLineSegment(sketch, "E324", {"start": v(6.36, 7.3) * mm, "end": v(6.6, 7.49) * mm});
            skLineSegment(sketch, "E325", {"start": v(6.6, 7.49) * mm, "end": v(6.93, 7.35) * mm});
            skLineSegment(sketch, "E326", {"start": v(6.93, 7.35) * mm, "end": v(7.36, 7.24) * mm});
            skLineSegment(sketch, "E327", {"start": v(7.36, 7.24) * mm, "end": v(7.96, 7.19) * mm});
            skLineSegment(sketch, "E328", {"start": v(7.96, 7.19) * mm, "end": v(8.1, 7.08) * mm});
            skLineSegment(sketch, "E329", {"start": v(8.1, 7.08) * mm, "end": v(8.03, 6.9) * mm});
            skLineSegment(sketch, "E330", {"start": v(8.03, 6.9) * mm, "end": v(8.26, 6.88) * mm});
            skLineSegment(sketch, "E331", {"start": v(8.26, 6.88) * mm, "end": v(8.44, 6.62) * mm});
            skLineSegment(sketch, "E332", {"start": v(8.44, 6.62) * mm, "end": v(8.46, 6.54) * mm});
            skLineSegment(sketch, "E333", {"start": v(8.46, 6.54) * mm, "end": v(8.77, 6.55) * mm});
            skLineSegment(sketch, "E334", {"start": v(8.77, 6.55) * mm, "end": v(8.88, 6.58) * mm});
            skLineSegment(sketch, "E335", {"start": v(8.88, 6.58) * mm, "end": v(9.1, 6.51) * mm});
            skLineSegment(sketch, "E336", {"start": v(9.1, 6.51) * mm, "end": v(9.14, 6.4) * mm});
            skLineSegment(sketch, "E337", {"start": v(9.14, 6.4) * mm, "end": v(9.3, 6.54) * mm});
            skLineSegment(sketch, "E338", {"start": v(9.3, 6.54) * mm, "end": v(9.47, 6.5) * mm});
            skLineSegment(sketch, "E339", {"start": v(9.47, 6.5) * mm, "end": v(9.6, 6.36) * mm});
            skLineSegment(sketch, "E340", {"start": v(9.6, 6.36) * mm, "end": v(9.71, 6.4) * mm});
            skLineSegment(sketch, "E341", {"start": v(9.71, 6.4) * mm, "end": v(10.32, 6.1) * mm});
            skLineSegment(sketch, "E342", {"start": v(10.32, 6.1) * mm, "end": v(10.34, 6.2) * mm});
            skLineSegment(sketch, "E343", {"start": v(10.34, 6.2) * mm, "end": v(10.43, 6.08) * mm});
            skLineSegment(sketch, "E344", {"start": v(10.43, 6.08) * mm, "end": v(10.49, 6.22) * mm});
            skLineSegment(sketch, "E345", {"start": v(10.49, 6.22) * mm, "end": v(10.64, 6.07) * mm});
            skLineSegment(sketch, "E346", {"start": v(10.64, 6.07) * mm, "end": v(10.8, 6.22) * mm});
            skLineSegment(sketch, "E347", {"start": v(10.8, 6.22) * mm, "end": v(10.84, 6.07) * mm});
            skLineSegment(sketch, "E348", {"start": v(10.84, 6.07) * mm, "end": v(11, 6.12) * mm});
            skLineSegment(sketch, "E349", {"start": v(11, 6.12) * mm, "end": v(11.07, 5.85) * mm});
            skLineSegment(sketch, "E350", {"start": v(11.07, 5.85) * mm, "end": v(11.18, 5.75) * mm});
            skLineSegment(sketch, "E351", {"start": v(11.18, 5.75) * mm, "end": v(11.33, 5.71) * mm});
            skLineSegment(sketch, "E352", {"start": v(11.33, 5.71) * mm, "end": v(11.37, 5.62) * mm});
            skLineSegment(sketch, "E353", {"start": v(11.37, 5.62) * mm, "end": v(11.34, 5.49) * mm});
            skLineSegment(sketch, "E354", {"start": v(11.34, 5.49) * mm, "end": v(11.38, 5.36) * mm});
            skLineSegment(sketch, "E355", {"start": v(11.38, 5.36) * mm, "end": v(11.5, 5.23) * mm});
            skLineSegment(sketch, "E356", {"start": v(11.5, 5.23) * mm, "end": v(11.6, 5.06) * mm});
            skLineSegment(sketch, "E357", {"start": v(11.6, 5.06) * mm, "end": v(11.8, 4.83) * mm});
            skLineSegment(sketch, "E358", {"start": v(11.8, 4.83) * mm, "end": v(11.13, 4.86) * mm});
            skLineSegment(sketch, "E359", {"start": v(11.13, 4.86) * mm, "end": v(11.1, 4.72) * mm});
            skLineSegment(sketch, "E360", {"start": v(11.1, 4.72) * mm, "end": v(10.95, 4.82) * mm});
            skLineSegment(sketch, "E361", {"start": v(10.95, 4.82) * mm, "end": v(10.95, 4.66) * mm});
            skLineSegment(sketch, "E362", {"start": v(10.95, 4.66) * mm, "end": v(10.84, 4.6) * mm});
            skLineSegment(sketch, "E363", {"start": v(10.84, 4.6) * mm, "end": v(11.07, 4.57) * mm});
            skLineSegment(sketch, "E364", {"start": v(11.07, 4.57) * mm, "end": v(10.92, 4.35) * mm});
            skLineSegment(sketch, "E365", {"start": v(10.92, 4.35) * mm, "end": v(10.94, 4.28) * mm});
            skLineSegment(sketch, "E366", {"start": v(10.94, 4.28) * mm, "end": v(11.22, 4.2) * mm});
            skLineSegment(sketch, "E367", {"start": v(11.22, 4.2) * mm, "end": v(11.16, 4.07) * mm});
            skLineSegment(sketch, "E368", {"start": v(11.16, 4.07) * mm, "end": v(11.2, 4.01) * mm});
            skLineSegment(sketch, "E369", {"start": v(11.2, 4.01) * mm, "end": v(11.4, 4.08) * mm});
            skLineSegment(sketch, "E370", {"start": v(11.4, 4.08) * mm, "end": v(11.56, 4.01) * mm});
            skLineSegment(sketch, "E371", {"start": v(11.56, 4.01) * mm, "end": v(11.67, 3.9) * mm});
            skLineSegment(sketch, "E372", {"start": v(11.67, 3.9) * mm, "end": v(11.9, 3.4) * mm});
            skLineSegment(sketch, "E373", {"start": v(11.9, 3.4) * mm, "end": v(11.98, 2.88) * mm});
            skLineSegment(sketch, "E374", {"start": v(11.98, 2.88) * mm, "end": v(11.98, 2.4) * mm});
            skLineSegment(sketch, "E375", {"start": v(11.98, 2.4) * mm, "end": v(11.87, 2.29) * mm});
            skLineSegment(sketch, "E376", {"start": v(11.87, 2.29) * mm, "end": v(11.93, 2.13) * mm});
            skLineSegment(sketch, "E377", {"start": v(11.93, 2.13) * mm, "end": v(11.76, 2) * mm});
            skLineSegment(sketch, "E378", {"start": v(11.76, 2) * mm, "end": v(11.83, 1.9) * mm});
            skLineSegment(sketch, "E379", {"start": v(11.83, 1.9) * mm, "end": v(11.82, 1.77) * mm});
            skLineSegment(sketch, "E380", {"start": v(11.82, 1.77) * mm, "end": v(11.73, 1.7) * mm});
            skLineSegment(sketch, "E381", {"start": v(11.73, 1.7) * mm, "end": v(11.83, 1.65) * mm});
            skLineSegment(sketch, "E382", {"start": v(11.83, 1.65) * mm, "end": v(11.85, 1.55) * mm});
            skLineSegment(sketch, "E383", {"start": v(11.85, 1.55) * mm, "end": v(11.76, 1.48) * mm});
            skLineSegment(sketch, "E384", {"start": v(11.76, 1.48) * mm, "end": v(11.86, 1.4) * mm});
            skLineSegment(sketch, "E385", {"start": v(11.86, 1.4) * mm, "end": v(11.86, 1.2) * mm});
            skLineSegment(sketch, "E386", {"start": v(11.86, 1.2) * mm, "end": v(11.62, 1.2) * mm});
            skLineSegment(sketch, "E387", {"start": v(11.62, 1.2) * mm, "end": v(11.23, 1.03) * mm});
            skLineSegment(sketch, "E388", {"start": v(11.23, 1.03) * mm, "end": v(11, 0.83) * mm});
            skLineSegment(sketch, "E389", {"start": v(11, 0.83) * mm, "end": v(11, 0.65) * mm});
            skLineSegment(sketch, "E390", {"start": v(11, 0.65) * mm, "end": v(11.06, 0.54) * mm});
            skLineSegment(sketch, "E391", {"start": v(11.06, 0.54) * mm, "end": v(11, 0.45) * mm});
            skLineSegment(sketch, "E392", {"start": v(11, 0.45) * mm, "end": v(11.08, 0.36) * mm});
            skLineSegment(sketch, "E393", {"start": v(11.08, 0.36) * mm, "end": v(11.09, 0.17) * mm});
            skLineSegment(sketch, "E394", {"start": v(11.09, 0.17) * mm, "end": v(11.16, 0.1) * mm});
            skLineSegment(sketch, "E395", {"start": v(11.16, 0.1) * mm, "end": v(11.17, 0) * mm});
            skLineSegment(sketch, "E396", {"start": v(11.17, 0) * mm, "end": v(11.2, -0.06) * mm});
            skLineSegment(sketch, "E397", {"start": v(11.2, -0.06) * mm, "end": v(11.22, -0.15) * mm});
            skLineSegment(sketch, "E398", {"start": v(11.22, -0.15) * mm, "end": v(11.28, -0.24) * mm});
            skLineSegment(sketch, "E399", {"start": v(11.28, -0.24) * mm, "end": v(11.23, -0.36) * mm});
            skLineSegment(sketch, "E400", {"start": v(11.23, -0.36) * mm, "end": v(11.02, -0.47) * mm});
            skLineSegment(sketch, "E401", {"start": v(11.02, -0.47) * mm, "end": v(10.9, -0.45) * mm});
            skLineSegment(sketch, "E402", {"start": v(10.9, -0.45) * mm, "end": v(10.81, -0.6) * mm});
            skLineSegment(sketch, "E403", {"start": v(10.81, -0.6) * mm, "end": v(10.64, -0.59) * mm});
            skLineSegment(sketch, "E404", {"start": v(10.64, -0.59) * mm, "end": v(10.5, -0.77) * mm});
            skLineSegment(sketch, "E405", {"start": v(10.5, -0.77) * mm, "end": v(10.35, -0.82) * mm});
            skLineSegment(sketch, "E406", {"start": v(10.35, -0.82) * mm, "end": v(10.27, -0.98) * mm});
            skLineSegment(sketch, "E407", {"start": v(10.27, -0.98) * mm, "end": v(10.12, -1.04) * mm});
            skLineSegment(sketch, "E408", {"start": v(10.12, -1.04) * mm, "end": v(10.11, -1.15) * mm});
            skLineSegment(sketch, "E409", {"start": v(10.11, -1.15) * mm, "end": v(10.06, -1.15) * mm});
            skLineSegment(sketch, "E410", {"start": v(10.06, -1.15) * mm, "end": v(10.1, -1.43) * mm});
            skLineSegment(sketch, "E411", {"start": v(10.1, -1.43) * mm, "end": v(9.97, -1.58) * mm});
            skLineSegment(sketch, "E412", {"start": v(9.97, -1.58) * mm, "end": v(9.83, -1.64) * mm});
            skLineSegment(sketch, "E413", {"start": v(9.83, -1.64) * mm, "end": v(10.06, -1.8) * mm});
            skLineSegment(sketch, "E414", {"start": v(10.06, -1.8) * mm, "end": v(10.1, -1.91) * mm});
            skLineSegment(sketch, "E415", {"start": v(10.1, -1.91) * mm, "end": v(10.05, -2) * mm});
            skLineSegment(sketch, "E416", {"start": v(10.05, -2) * mm, "end": v(9.95, -2.1) * mm});
            skLineSegment(sketch, "E417", {"start": v(9.95, -2.1) * mm, "end": v(10.13, -2.05) * mm});
            skLineSegment(sketch, "E418", {"start": v(10.13, -2.05) * mm, "end": v(10.24, -2.1) * mm});
            skLineSegment(sketch, "E419", {"start": v(10.24, -2.1) * mm, "end": v(10.26, -2.2) * mm});
            skLineSegment(sketch, "E420", {"start": v(10.26, -2.2) * mm, "end": v(10.26, -2.37) * mm});
            skLineSegment(sketch, "E421", {"start": v(10.26, -2.37) * mm, "end": v(10.42, -2.2) * mm});
            skLineSegment(sketch, "E422", {"start": v(10.42, -2.2) * mm, "end": v(10.55, -2.22) * mm});
            skLineSegment(sketch, "E423", {"start": v(10.55, -2.22) * mm, "end": v(10.66, -2.32) * mm});
            skLineSegment(sketch, "E424", {"start": v(10.66, -2.32) * mm, "end": v(10.7, -2.38) * mm});
            skLineSegment(sketch, "E425", {"start": v(10.7, -2.38) * mm, "end": v(10.86, -2.36) * mm});
            skLineSegment(sketch, "E426", {"start": v(10.86, -2.36) * mm, "end": v(11.02, -2.42) * mm});
            skLineSegment(sketch, "E427", {"start": v(11.02, -2.42) * mm, "end": v(11.14, -2.5) * mm});
            skLineSegment(sketch, "E428", {"start": v(11.14, -2.5) * mm, "end": v(11.58, -2.1) * mm});
            skLineSegment(sketch, "E429", {"start": v(11.58, -2.1) * mm, "end": v(11.94, -1.29) * mm});
            skLineSegment(sketch, "E430", {"start": v(11.94, -1.29) * mm, "end": v(12.1, -1.2) * mm});
            skLineSegment(sketch, "E431", {"start": v(12.1, -1.2) * mm, "end": v(12.2, -1.22) * mm});
            skLineSegment(sketch, "E432", {"start": v(12.2, -1.22) * mm, "end": v(12.18, -0.93) * mm});
            skLineSegment(sketch, "E433", {"start": v(12.18, -0.93) * mm, "end": v(12.28, -0.78) * mm});
            skLineSegment(sketch, "E434", {"start": v(12.28, -0.78) * mm, "end": v(12.45, -0.71) * mm});
            skLineSegment(sketch, "E435", {"start": v(12.45, -0.71) * mm, "end": v(12.63, -0.73) * mm});
            skLineSegment(sketch, "E436", {"start": v(12.63, -0.73) * mm, "end": v(12.4, -0.59) * mm});
            skLineSegment(sketch, "E437", {"start": v(12.4, -0.59) * mm, "end": v(12.45, -0.44) * mm});
            skLineSegment(sketch, "E438", {"start": v(12.45, -0.44) * mm, "end": v(12.77, -0.39) * mm});
            skLineSegment(sketch, "E439", {"start": v(12.77, -0.39) * mm, "end": v(13.14, -0.37) * mm});
            skLineSegment(sketch, "E440", {"start": v(13.14, -0.37) * mm, "end": v(13.38, -0.25) * mm});
            skLineSegment(sketch, "E441", {"start": v(13.38, -0.25) * mm, "end": v(13.87, 0.17) * mm});
            skLineSegment(sketch, "E442", {"start": v(13.87, 0.17) * mm, "end": v(14.4, -0.26) * mm});
            skLineSegment(sketch, "E443", {"start": v(14.4, -0.26) * mm, "end": v(14.41, -0.38) * mm});
            skLineSegment(sketch, "E444", {"start": v(14.41, -0.38) * mm, "end": v(14.35, -0.43) * mm});
            skLineSegment(sketch, "E445", {"start": v(14.35, -0.43) * mm, "end": v(14.62, -0.6) * mm});
            skLineSegment(sketch, "E446", {"start": v(14.62, -0.6) * mm, "end": v(14.6, -0.82) * mm});
            skLineSegment(sketch, "E447", {"start": v(14.6, -0.82) * mm, "end": v(14.73, -0.83) * mm});
            skLineSegment(sketch, "E448", {"start": v(14.73, -0.83) * mm, "end": v(14.73, -1.06) * mm});
            skLineSegment(sketch, "E449", {"start": v(14.73, -1.06) * mm, "end": v(14.85, -1.07) * mm});
            skLineSegment(sketch, "E450", {"start": v(14.85, -1.07) * mm, "end": v(15.06, -1.86) * mm});
            skLineSegment(sketch, "E451", {"start": v(15.06, -1.86) * mm, "end": v(15.2, -2.46) * mm});
            skLineSegment(sketch, "E452", {"start": v(15.2, -2.46) * mm, "end": v(15.14, -2.64) * mm});
            skLineSegment(sketch, "E453", {"start": v(15.14, -2.64) * mm, "end": v(15.24, -2.73) * mm});
            skLineSegment(sketch, "E454", {"start": v(15.24, -2.73) * mm, "end": v(15.24, -2.83) * mm});
            skLineSegment(sketch, "E455", {"start": v(15.24, -2.83) * mm, "end": v(15.22, -2.92) * mm});
            skLineSegment(sketch, "E456", {"start": v(15.22, -2.92) * mm, "end": v(15.12, -3) * mm});
            skLineSegment(sketch, "E457", {"start": v(15.12, -3) * mm, "end": v(15.3, -3.12) * mm});
            skLineSegment(sketch, "E458", {"start": v(15.3, -3.12) * mm, "end": v(15.27, -3.22) * mm});
            skLineSegment(sketch, "E459", {"start": v(15.27, -3.22) * mm, "end": v(15.34, -3.28) * mm});
            skLineSegment(sketch, "E460", {"start": v(15.34, -3.28) * mm, "end": v(15.3, -3.34) * mm});
            skLineSegment(sketch, "E461", {"start": v(15.3, -3.34) * mm, "end": v(15.41, -3.42) * mm});
            skLineSegment(sketch, "E462", {"start": v(15.41, -3.42) * mm, "end": v(15.38, -3.5) * mm});
            skLineSegment(sketch, "E463", {"start": v(15.38, -3.5) * mm, "end": v(15.5, -3.6) * mm});
            skLineSegment(sketch, "E464", {"start": v(15.5, -3.6) * mm, "end": v(15.49, -3.9) * mm});
            skLineSegment(sketch, "E465", {"start": v(15.49, -3.9) * mm, "end": v(15.59, -4.04) * mm});
            skLineSegment(sketch, "E466", {"start": v(15.59, -4.04) * mm, "end": v(15.66, -4.25) * mm});
            skLineSegment(sketch, "E467", {"start": v(15.66, -4.25) * mm, "end": v(15.83, -4.28) * mm});
            skLineSegment(sketch, "E468", {"start": v(15.83, -4.28) * mm, "end": v(16, -4.46) * mm});
            skLineSegment(sketch, "E469", {"start": v(16, -4.46) * mm, "end": v(16.2, -4.6) * mm});
            skLineSegment(sketch, "E470", {"start": v(16.2, -4.6) * mm, "end": v(16.15, -5.8) * mm});
            skLineSegment(sketch, "E471", {"start": v(16.15, -5.8) * mm, "end": v(16.15, -6.2) * mm});
            skLineSegment(sketch, "E472", {"start": v(16.15, -6.2) * mm, "end": v(16.1, -6.72) * mm});
            skLineSegment(sketch, "E473", {"start": v(16.1, -6.72) * mm, "end": v(16.02, -6.88) * mm});
            skLineSegment(sketch, "E474", {"start": v(16.02, -6.88) * mm, "end": v(15.87, -6.9) * mm});
            skLineSegment(sketch, "E475", {"start": v(15.87, -6.9) * mm, "end": v(15.85, -6.8) * mm});
            skLineSegment(sketch, "E476", {"start": v(15.85, -6.8) * mm, "end": v(15.65, -6.76) * mm});
            skLineSegment(sketch, "E477", {"start": v(15.65, -6.76) * mm, "end": v(15.64, -6.68) * mm});
            skLineSegment(sketch, "E478", {"start": v(15.64, -6.68) * mm, "end": v(15.51, -6.67) * mm});
            skLineSegment(sketch, "E479", {"start": v(15.51, -6.67) * mm, "end": v(15.45, -6.44) * mm});
            skLineSegment(sketch, "E480", {"start": v(15.45, -6.44) * mm, "end": v(15.28, -6.54) * mm});
            skLineSegment(sketch, "E481", {"start": v(15.28, -6.54) * mm, "end": v(15.2, -6.53) * mm});
            skLineSegment(sketch, "E482", {"start": v(15.2, -6.53) * mm, "end": v(15.1, -6.4) * mm});
            skLineSegment(sketch, "E483", {"start": v(15.1, -6.4) * mm, "end": v(15.08, -6.46) * mm});
            skLineSegment(sketch, "E484", {"start": v(15.08, -6.46) * mm, "end": v(15, -6.52) * mm});
            skLineSegment(sketch, "E485", {"start": v(15, -6.52) * mm, "end": v(14.86, -6.54) * mm});
            skLineSegment(sketch, "E486", {"start": v(14.86, -6.54) * mm, "end": v(14.8, -6.5) * mm});
            skLineSegment(sketch, "E487", {"start": v(14.8, -6.5) * mm, "end": v(14.79, -6.74) * mm});
            skLineSegment(sketch, "E488", {"start": v(14.79, -6.74) * mm, "end": v(14.7, -6.88) * mm});
            skLineSegment(sketch, "E489", {"start": v(14.7, -6.88) * mm, "end": v(14.6, -6.99) * mm});
            skLineSegment(sketch, "E490", {"start": v(14.6, -6.99) * mm, "end": v(14.44, -7.04) * mm});
            skLineSegment(sketch, "E491", {"start": v(14.44, -7.04) * mm, "end": v(14.58, -7.14) * mm});
            skLineSegment(sketch, "E492", {"start": v(14.58, -7.14) * mm, "end": v(14.54, -7.24) * mm});
            skLineSegment(sketch, "E493", {"start": v(14.54, -7.24) * mm, "end": v(14.59, -7.35) * mm});
            skLineSegment(sketch, "E494", {"start": v(14.59, -7.35) * mm, "end": v(14.54, -7.43) * mm});
            skLineSegment(sketch, "E495", {"start": v(14.54, -7.43) * mm, "end": v(14.68, -7.57) * mm});
            skLineSegment(sketch, "E496", {"start": v(14.68, -7.57) * mm, "end": v(14.78, -7.88) * mm});
            skLineSegment(sketch, "E497", {"start": v(14.78, -7.88) * mm, "end": v(14.81, -8.32) * mm});
            skLineSegment(sketch, "E498", {"start": v(14.81, -8.32) * mm, "end": v(14.64, -8.56) * mm});
            skLineSegment(sketch, "E499", {"start": v(14.64, -8.56) * mm, "end": v(14.42, -8.91) * mm});
            skLineSegment(sketch, "E500", {"start": v(14.42, -8.91) * mm, "end": v(13.9, -9.78) * mm});
            skLineSegment(sketch, "E501", {"start": v(13.9, -9.78) * mm, "end": v(13.72, -10.24) * mm});
            skLineSegment(sketch, "E502", {"start": v(13.72, -10.24) * mm, "end": v(13.72, -10.35) * mm});
            skLineSegment(sketch, "E503", {"start": v(13.72, -10.35) * mm, "end": v(13.65, -10.4) * mm});
            skLineSegment(sketch, "E504", {"start": v(13.65, -10.4) * mm, "end": v(13.66, -10.45) * mm});
            skLineSegment(sketch, "E505", {"start": v(13.66, -10.45) * mm, "end": v(13.48, -10.56) * mm});
            skLineSegment(sketch, "E506", {"start": v(13.48, -10.56) * mm, "end": v(13.48, -10.81) * mm});
            skLineSegment(sketch, "E507", {"start": v(13.48, -10.81) * mm, "end": v(13.37, -11.07) * mm});
            skLineSegment(sketch, "E508", {"start": v(13.37, -11.07) * mm, "end": v(13.07, -11.73) * mm});
            skLineSegment(sketch, "E509", {"start": v(13.07, -11.73) * mm, "end": v(8.2, -12.53) * mm});
            skLineSegment(sketch, "E510", {"start": v(8.2, -12.53) * mm, "end": v(8.12, -12.1) * mm});
            skLineSegment(sketch, "E511", {"start": v(8.12, -12.1) * mm, "end": v(0.96, -12.92) * mm});
            skLineSegment(sketch, "E512", {"start": v(0.96, -12.92) * mm, "end": v(1.35, -12.58) * mm});
            skLineSegment(sketch, "E513", {"start": v(1.35, -12.58) * mm, "end": v(1.56, -12.53) * mm});
            skLineSegment(sketch, "E514", {"start": v(1.56, -12.53) * mm, "end": v(1.68, -12.58) * mm});
            skLineSegment(sketch, "E515", {"start": v(1.68, -12.58) * mm, "end": v(1.7, -12.4) * mm});
            skLineSegment(sketch, "E516", {"start": v(1.7, -12.4) * mm, "end": v(1.77, -12.28) * mm});
            skLineSegment(sketch, "E517", {"start": v(1.77, -12.28) * mm, "end": v(1.86, -12.3) * mm});
            skLineSegment(sketch, "E518", {"start": v(1.86, -12.3) * mm, "end": v(1.82, -12.18) * mm});
            skLineSegment(sketch, "E519", {"start": v(1.82, -12.18) * mm, "end": v(2.03, -12.12) * mm});
            skLineSegment(sketch, "E520", {"start": v(2.03, -12.12) * mm, "end": v(1.82, -11.96) * mm});
            skLineSegment(sketch, "E521", {"start": v(1.82, -11.96) * mm, "end": v(1.82, -11.82) * mm});
            skLineSegment(sketch, "E522", {"start": v(1.82, -11.82) * mm, "end": v(1.97, -11.6) * mm});
            skLineSegment(sketch, "E523", {"start": v(1.97, -11.6) * mm, "end": v(1.84, -11.6) * mm});
            skLineSegment(sketch, "E524", {"start": v(1.84, -11.6) * mm, "end": v(1.82, -11.5) * mm});
            skLineSegment(sketch, "E525", {"start": v(1.82, -11.5) * mm, "end": v(1.94, -11.37) * mm});
            skLineSegment(sketch, "E526", {"start": v(1.94, -11.37) * mm, "end": v(1.87, -11.18) * mm});
            skLineSegment(sketch, "E527", {"start": v(1.87, -11.18) * mm, "end": v(2.07, -11.22) * mm});
            skLineSegment(sketch, "E528", {"start": v(2.07, -11.22) * mm, "end": v(1.95, -11.06) * mm});
            skLineSegment(sketch, "E529", {"start": v(1.95, -11.06) * mm, "end": v(2.16, -10.97) * mm});
            skLineSegment(sketch, "E530", {"start": v(2.16, -10.97) * mm, "end": v(2.04, -10.84) * mm});
            skLineSegment(sketch, "E531", {"start": v(2.04, -10.84) * mm, "end": v(2.3, -10.4) * mm});
            skLineSegment(sketch, "E532", {"start": v(2.3, -10.4) * mm, "end": v(2.48, -10.42) * mm});
            skLineSegment(sketch, "E533", {"start": v(2.48, -10.42) * mm, "end": v(2.48, -10.27) * mm});
            skLineSegment(sketch, "E534", {"start": v(2.48, -10.27) * mm, "end": v(2.62, -10.32) * mm});
            skLineSegment(sketch, "E535", {"start": v(2.62, -10.32) * mm, "end": v(2.57, -10.1) * mm});
            skLineSegment(sketch, "E536", {"start": v(2.57, -10.1) * mm, "end": v(2.8, -10.1) * mm});
            skLineSegment(sketch, "E537", {"start": v(2.8, -10.1) * mm, "end": v(2.63, -9.9) * mm});
            skLineSegment(sketch, "E538", {"start": v(2.63, -9.9) * mm, "end": v(2.85, -9.81) * mm});
            skLineSegment(sketch, "E539", {"start": v(2.85, -9.81) * mm, "end": v(2.63, -9.72) * mm});
            skLineSegment(sketch, "E540", {"start": v(2.63, -9.72) * mm, "end": v(2.82, -9.59) * mm});
            skLineSegment(sketch, "E541", {"start": v(2.82, -9.59) * mm, "end": v(2.64, -9.53) * mm});
            skLineSegment(sketch, "E542", {"start": v(2.64, -9.53) * mm, "end": v(2.66, -9.22) * mm});
            skLineSegment(sketch, "E543", {"start": v(2.66, -9.22) * mm, "end": v(2.6, -9.06) * mm});
            skLineSegment(sketch, "E544", {"start": v(2.6, -9.06) * mm, "end": v(2.7, -8.83) * mm});
            skLineSegment(sketch, "E545", {"start": v(2.7, -8.83) * mm, "end": v(2.57, -8.78) * mm});
            skLineSegment(sketch, "E546", {"start": v(2.57, -8.78) * mm, "end": v(2.67, -8.67) * mm});
            skLineSegment(sketch, "E547", {"start": v(2.67, -8.67) * mm, "end": v(2.58, -8.64) * mm});
            skLineSegment(sketch, "E548", {"start": v(2.58, -8.64) * mm, "end": v(2.56, -8.46) * mm});
            skLineSegment(sketch, "E549", {"start": v(2.56, -8.46) * mm, "end": v(2.62, -8.37) * mm});
            skLineSegment(sketch, "E550", {"start": v(2.62, -8.37) * mm, "end": v(2.57, -8.22) * mm});
            skLineSegment(sketch, "E551", {"start": v(2.57, -8.22) * mm, "end": v(2.5, -7.7) * mm});
            skLineSegment(sketch, "E552", {"start": v(2.5, -7.7) * mm, "end": v(2.42, -7.5) * mm});
            skLineSegment(sketch, "E553", {"start": v(2.42, -7.5) * mm, "end": v(2.43, -7.34) * mm});
            skLineSegment(sketch, "E554", {"start": v(2.43, -7.34) * mm, "end": v(2.5, -7.3) * mm});
            skLineSegment(sketch, "E555", {"start": v(2.5, -7.3) * mm, "end": v(2.41, -7.22) * mm});
            skLineSegment(sketch, "E556", {"start": v(2.41, -7.22) * mm, "end": v(2.42, -7.14) * mm});
            skLineSegment(sketch, "E557", {"start": v(2.42, -7.14) * mm, "end": v(2.52, -7.11) * mm});
            skLineSegment(sketch, "E558", {"start": v(2.52, -7.11) * mm, "end": v(2.4, -7.07) * mm});
            skLineSegment(sketch, "E559", {"start": v(2.4, -7.07) * mm, "end": v(2.4, -6.97) * mm});
            skLineSegment(sketch, "E560", {"start": v(2.4, -6.97) * mm, "end": v(2.48, -6.92) * mm});
            skLineSegment(sketch, "E561", {"start": v(2.48, -6.92) * mm, "end": v(2.39, -6.85) * mm});
            skLineSegment(sketch, "E562", {"start": v(2.39, -6.85) * mm, "end": v(2.37, -6.4) * mm});
            skLineSegment(sketch, "E563", {"start": v(2.37, -6.4) * mm, "end": v(2.47, -6.36) * mm});
            skLineSegment(sketch, "E564", {"start": v(2.47, -6.36) * mm, "end": v(2.4, -6.29) * mm});
            skLineSegment(sketch, "E565", {"start": v(2.4, -6.29) * mm, "end": v(2.5, -6.23) * mm});
            skLineSegment(sketch, "E566", {"start": v(2.5, -6.23) * mm, "end": v(2.34, -6.12) * mm});
            skLineSegment(sketch, "E567", {"start": v(2.34, -6.12) * mm, "end": v(2.49, -6.08) * mm});
            skLineSegment(sketch, "E568", {"start": v(2.49, -6.08) * mm, "end": v(2.32, -5.97) * mm});
            skLineSegment(sketch, "E569", {"start": v(2.32, -5.97) * mm, "end": v(2.3, -5.89) * mm});
            skLineSegment(sketch, "E570", {"start": v(2.3, -5.89) * mm, "end": v(2.44, -5.76) * mm});
            skLineSegment(sketch, "E571", {"start": v(2.44, -5.76) * mm, "end": v(2.22, -5.78) * mm});
            skLineSegment(sketch, "E572", {"start": v(2.22, -5.78) * mm, "end": v(2.34, -5.63) * mm});
            skLineSegment(sketch, "E573", {"start": v(2.34, -5.63) * mm, "end": v(2.2, -5.64) * mm});
            skLineSegment(sketch, "E574", {"start": v(2.2, -5.64) * mm, "end": v(2.27, -5.44) * mm});
            skLineSegment(sketch, "E575", {"start": v(2.27, -5.44) * mm, "end": v(2.1, -5.53) * mm});
            skLineSegment(sketch, "E576", {"start": v(2.1, -5.53) * mm, "end": v(2.16, -5.26) * mm});
            skLineSegment(sketch, "E577", {"start": v(2.16, -5.26) * mm, "end": v(2.01, -5.42) * mm});
            skLineSegment(sketch, "E578", {"start": v(2.01, -5.42) * mm, "end": v(2.03, -5.2) * mm});
            skLineSegment(sketch, "E579", {"start": v(2.03, -5.2) * mm, "end": v(1.87, -5.32) * mm});
            skLineSegment(sketch, "E580", {"start": v(1.87, -5.32) * mm, "end": v(1.34, -4.24) * mm});
            skLineSegment(sketch, "E581", {"start": v(1.34, -4.24) * mm, "end": v(1.06, -3.67) * mm});
            skLineSegment(sketch, "E582", {"start": v(1.06, -3.67) * mm, "end": v(1.04, -3.56) * mm});
            skLineSegment(sketch, "E583", {"start": v(1.04, -3.56) * mm, "end": v(1.05, -3.44) * mm});
            skLineSegment(sketch, "E584", {"start": v(1.05, -3.44) * mm, "end": v(0.93, -3.38) * mm});
            skLineSegment(sketch, "E585", {"start": v(0.93, -3.38) * mm, "end": v(0.93, -3.25) * mm});
            skLineSegment(sketch, "E586", {"start": v(0.93, -3.25) * mm, "end": v(0.98, -3.04) * mm});
            skLineSegment(sketch, "E587", {"start": v(0.98, -3.04) * mm, "end": v(1.3, -2.19) * mm});
            skLineSegment(sketch, "E588", {"start": v(1.3, -2.19) * mm, "end": v(1.28, -2.02) * mm});
            skLineSegment(sketch, "E589", {"start": v(1.28, -2.02) * mm, "end": v(1.17, -1.92) * mm});
            skLineSegment(sketch, "E590", {"start": v(1.17, -1.92) * mm, "end": v(1.1, -1.8) * mm});
            skLineSegment(sketch, "E591", {"start": v(1.1, -1.8) * mm, "end": v(1.1, -1.72) * mm});
            skLineSegment(sketch, "E592", {"start": v(1.1, -1.72) * mm, "end": v(1.1, -1.58) * mm});
            skLineSegment(sketch, "E593", {"start": v(1.1, -1.58) * mm, "end": v(1, -1.57) * mm});
            skLineSegment(sketch, "E594", {"start": v(1, -1.57) * mm, "end": v(0.93, -1.5) * mm});
            skLineSegment(sketch, "E595", {"start": v(0.93, -1.5) * mm, "end": v(0.92, -1.38) * mm});
            skLineSegment(sketch, "E596", {"start": v(0.92, -1.38) * mm, "end": v(1.19, -0.9) * mm});
            skLineSegment(sketch, "E597", {"start": v(1.19, -0.9) * mm, "end": v(1.22, -0.81) * mm});
            skLineSegment(sketch, "E598", {"start": v(1.22, -0.81) * mm, "end": v(1.3, -0.76) * mm});
            skLineSegment(sketch, "E599", {"start": v(1.3, -0.76) * mm, "end": v(1.3, -0.64) * mm});
            skLineSegment(sketch, "E600", {"start": v(1.3, -0.64) * mm, "end": v(1.38, -0.57) * mm});
            skLineSegment(sketch, "E601", {"start": v(1.38, -0.57) * mm, "end": v(1.4, -0.57) * mm});
            skLineSegment(sketch, "E602", {"start": v(1.4, -0.57) * mm, "end": v(1.37, -0.5) * mm});
            skLineSegment(sketch, "E603", {"start": v(1.37, -0.5) * mm, "end": v(1.49, -0.25) * mm});
            skLineSegment(sketch, "E604", {"start": v(1.49, -0.25) * mm, "end": v(1.48, -0.1) * mm});
            skLineSegment(sketch, "E605", {"start": v(1.48, -0.1) * mm, "end": v(1.5, 0.11) * mm});
            skLineSegment(sketch, "E606", {"start": v(1.5, 0.11) * mm, "end": v(1.51, 0.32) * mm});
            skLineSegment(sketch, "E607", {"start": v(1.51, 0.32) * mm, "end": v(1.45, 0.42) * mm});
            skLineSegment(sketch, "E608", {"start": v(1.45, 0.42) * mm, "end": v(1.55, 0.56) * mm});
            skLineSegment(sketch, "E609", {"start": v(1.55, 0.56) * mm, "end": v(1.57, 0.64) * mm});
            skLineSegment(sketch, "E610", {"start": v(1.57, 0.64) * mm, "end": v(1.5, 0.7) * mm});
            skLineSegment(sketch, "E611", {"start": v(1.5, 0.7) * mm, "end": v(1.51, 0.76) * mm});
            skLineSegment(sketch, "E612", {"start": v(1.51, 0.76) * mm, "end": v(1.58, 0.76) * mm});
            skLineSegment(sketch, "E613", {"start": v(1.58, 0.76) * mm, "end": v(1.54, 0.82) * mm});
            skLineSegment(sketch, "E614", {"start": v(1.54, 0.82) * mm, "end": v(1.55, 0.87) * mm});
            skLineSegment(sketch, "E615", {"start": v(1.55, 0.87) * mm, "end": v(1.6, 0.85) * mm});
            skLineSegment(sketch, "E616", {"start": v(1.6, 0.85) * mm, "end": v(1.5, 1.19) * mm});
            skLineSegment(sketch, "E617", {"start": v(1.5, 1.19) * mm, "end": v(1.34, 1.35) * mm});
            skLineSegment(sketch, "E618", {"start": v(1.34, 1.35) * mm, "end": v(1.39, 1.77) * mm});
            skLineSegment(sketch, "E619", {"start": v(1.39, 1.77) * mm, "end": v(1.3, 1.88) * mm});
            skLineSegment(sketch, "E620", {"start": v(1.3, 1.88) * mm, "end": v(1.36, 1.95) * mm});
            skLineSegment(sketch, "E621", {"start": v(1.36, 1.95) * mm, "end": v(1.4, 2.03) * mm});
            skLineSegment(sketch, "E622", {"start": v(1.4, 2.03) * mm, "end": v(1.56, 2.06) * mm});
            skLineSegment(sketch, "E623", {"start": v(1.56, 2.06) * mm, "end": v(1.56, 2.12) * mm});
            skLineSegment(sketch, "E624", {"start": v(1.56, 2.12) * mm, "end": v(1.66, 2.2) * mm});
            skLineSegment(sketch, "E625", {"start": v(1.66, 2.2) * mm, "end": v(1.92, 2.36) * mm});
            skLineSegment(sketch, "E626", {"start": v(1.92, 2.36) * mm, "end": v(1.97, 2.6) * mm});
            skLineSegment(sketch, "E627", {"start": v(1.97, 2.6) * mm, "end": v(2.1, 2.8) * mm});
            skLineSegment(sketch, "E628", {"start": v(2.1, 2.8) * mm, "end": v(2.1, 2.85) * mm});
            skLineSegment(sketch, "E629", {"start": v(2.1, 2.85) * mm, "end": v(2.06, 2.9) * mm});
            skLineSegment(sketch, "E630", {"start": v(2.06, 2.9) * mm, "end": v(2.1, 2.93) * mm});
            skLineSegment(sketch, "E631", {"start": v(2.1, 2.93) * mm, "end": v(2.18, 2.92) * mm});
            skLineSegment(sketch, "E632", {"start": v(2.18, 2.92) * mm, "end": v(2.18, 3.06) * mm});
            skLineSegment(sketch, "E633", {"start": v(2.18, 3.06) * mm, "end": v(2.24, 3.07) * mm});
            skLineSegment(sketch, "E634", {"start": v(2.24, 3.07) * mm, "end": v(2.5, 3.42) * mm});
            skLineSegment(sketch, "E635", {"start": v(2.5, 3.42) * mm, "end": v(2.9, 3.55) * mm});
            skLineSegment(sketch, "E636", {"start": v(2.9, 3.55) * mm, "end": v(3.38, 4.43) * mm});
            skLineSegment(sketch, "E637", {"start": v(3.38, 4.43) * mm, "end": v(3.42, 4.47) * mm});
            skLineSegment(sketch, "E638", {"start": v(3.42, 4.47) * mm, "end": v(3.45, 4.44) * mm});
            skLineSegment(sketch, "E639", {"start": v(3.45, 4.44) * mm, "end": v(3.29, 3.16) * mm});
            skLineSegment(sketch, "E640", {"start": v(3.29, 3.16) * mm, "end": v(3.33, 3.12) * mm});
            skLineSegment(sketch, "E641", {"start": v(3.33, 3.12) * mm, "end": v(3.33, 3.06) * mm});
            skLineSegment(sketch, "E642", {"start": v(3.33, 3.06) * mm, "end": v(3.5, 2.95) * mm});
            skLineSegment(sketch, "E643", {"start": v(3.5, 2.95) * mm, "end": v(3.51, 2.68) * mm});
            skLineSegment(sketch, "E644", {"start": v(3.51, 2.68) * mm, "end": v(3.7, 2.36) * mm});
            skLineSegment(sketch, "E645", {"start": v(3.7, 2.36) * mm, "end": v(4.5, 3.23) * mm});
            skLineSegment(sketch, "E646", {"start": v(4.5, 3.23) * mm, "end": v(4.52, 3.28) * mm});
            skLineSegment(sketch, "E647", {"start": v(4.52, 3.28) * mm, "end": v(4.4, 3.26) * mm});
            skLineSegment(sketch, "E648", {"start": v(4.4, 3.26) * mm, "end": v(4.32, 3.25) * mm});
            skLineSegment(sketch, "E649", {"start": v(4.32, 3.25) * mm, "end": v(4.3, 3.33) * mm});
            skLineSegment(sketch, "E650", {"start": v(4.3, 3.33) * mm, "end": v(4.4, 3.46) * mm});
            skLineSegment(sketch, "E651", {"start": v(4.4, 3.46) * mm, "end": v(4.4, 3.64) * mm});
            skLineSegment(sketch, "E652", {"start": v(4.4, 3.64) * mm, "end": v(4.29, 3.75) * mm});
            skLineSegment(sketch, "E653", {"start": v(4.29, 3.75) * mm, "end": v(4.12, 3.83) * mm});
            skLineSegment(sketch, "E654", {"start": v(4.12, 3.83) * mm, "end": v(4.1, 3.93) * mm});
            skLineSegment(sketch, "E655", {"start": v(4.1, 3.93) * mm, "end": v(4.29, 3.98) * mm});
            skLineSegment(sketch, "E656", {"start": v(4.29, 3.98) * mm, "end": v(4.15, 4.07) * mm});
            skLineSegment(sketch, "E657", {"start": v(4.15, 4.07) * mm, "end": v(4.15, 4.15) * mm});
            skLineSegment(sketch, "E658", {"start": v(4.15, 4.15) * mm, "end": v(4.24, 4.16) * mm});
            skLineSegment(sketch, "E659", {"start": v(4.24, 4.16) * mm, "end": v(4.14, 4.4) * mm});
            skLineSegment(sketch, "E660", {"start": v(4.14, 4.4) * mm, "end": v(4.18, 4.47) * mm});
            skLineSegment(sketch, "E661", {"start": v(4.18, 4.47) * mm, "end": v(4.12, 4.57) * mm});
            skLineSegment(sketch, "E662", {"start": v(4.12, 4.57) * mm, "end": v(4.18, 4.76) * mm});
            skLineSegment(sketch, "E663", {"start": v(4.18, 4.76) * mm, "end": v(4.16, 4.98) * mm});
            skLineSegment(sketch, "E664", {"start": v(4.16, 4.98) * mm, "end": v(4.23, 5.1) * mm});
            skLineSegment(sketch, "E665", {"start": v(4.23, 5.1) * mm, "end": v(4.24, 5.2) * mm});
            skLineSegment(sketch, "E666", {"start": v(4.24, 5.2) * mm, "end": v(4.4, 5.32) * mm});
            skLineSegment(sketch, "E667", {"start": v(4.4, 5.32) * mm, "end": v(4.7, 5.5) * mm});
            skLineSegment(sketch, "E668", {"start": v(4.7, 5.5) * mm, "end": v(5.8, 5.91) * mm});
            skLineSegment(sketch, "E669", {"start": v(5.8, 5.91) * mm, "end": v(5.55, 6.07) * mm});
            skLineSegment(sketch, "E670", {"start": v(5.55, 6.07) * mm, "end": v(5.43, 6.06) * mm});
            skLineSegment(sketch, "E671", {"start": v(5.43, 6.06) * mm, "end": v(5.31, 6) * mm});
            skLineSegment(sketch, "E672", {"start": v(5.31, 6) * mm, "end": v(5.14, 6.25) * mm});
            skLineSegment(sketch, "E673", {"start": v(5.14, 6.25) * mm, "end": v(4.94, 6.26) * mm});
            skLineSegment(sketch, "E674", {"start": v(4.94, 6.26) * mm, "end": v(4.78, 6.2) * mm});
            skLineSegment(sketch, "E675", {"start": v(4.78, 6.2) * mm, "end": v(4.76, 6.43) * mm});
            skLineSegment(sketch, "E676", {"start": v(4.76, 6.43) * mm, "end": v(4.65, 6.41) * mm});
            skLineSegment(sketch, "E677", {"start": v(4.65, 6.41) * mm, "end": v(4.6, 6.45) * mm});
            skLineSegment(sketch, "E678", {"start": v(4.6, 6.45) * mm, "end": v(4.74, 6.54) * mm});
            skLineSegment(sketch, "E679", {"start": v(4.74, 6.54) * mm, "end": v(4.58, 6.55) * mm});
            skLineSegment(sketch, "E680", {"start": v(4.58, 6.55) * mm, "end": v(4.57, 6.64) * mm});
            skLineSegment(sketch, "E681", {"start": v(4.57, 6.64) * mm, "end": v(4.73, 6.7) * mm});
            skLineSegment(sketch, "E682", {"start": v(4.73, 6.7) * mm, "end": v(4.82, 6.8) * mm});
            skLineSegment(sketch, "E683", {"start": v(4.82, 6.8) * mm, "end": v(4.84, 6.88) * mm});
            skLineSegment(sketch, "E684", {"start": v(4.84, 6.88) * mm, "end": v(4.82, 6.96) * mm});
            skLineSegment(sketch, "E685", {"start": v(4.82, 6.96) * mm, "end": v(4.72, 7.08) * mm});
            skLineSegment(sketch, "E686", {"start": v(4.72, 7.08) * mm, "end": v(4.61, 7.16) * mm});
            skLineSegment(sketch, "E687", {"start": v(4.61, 7.16) * mm, "end": v(4.62, 7.21) * mm});
            skLineSegment(sketch, "E688", {"start": v(4.62, 7.21) * mm, "end": v(4.99, 7.18) * mm});
            skLineSegment(sketch, "E689", {"start": v(4.99, 7.18) * mm, "end": v(5.02, 7.2) * mm});
            skLineSegment(sketch, "E690", {"start": v(5.02, 7.2) * mm, "end": v(5.02, 7.29) * mm});
            skLineSegment(sketch, "E691", {"start": v(5.02, 7.29) * mm, "end": v(4.9, 7.46) * mm});
            skLineSegment(sketch, "E692", {"start": v(4.9, 7.46) * mm, "end": v(4.91, 7.52) * mm});
            skLineSegment(sketch, "E693", {"start": v(4.91, 7.52) * mm, "end": v(4.96, 7.53) * mm});
            skLineSegment(sketch, "E694", {"start": v(4.96, 7.53) * mm, "end": v(5.13, 7.32) * mm});
            skLineSegment(sketch, "E695", {"start": v(5.13, 7.32) * mm, "end": v(5.22, 7.63) * mm});
            skLineSegment(sketch, "E696", {"start": v(5.22, 7.63) * mm, "end": v(5.28, 7.62) * mm});
            skLineSegment(sketch, "E697", {"start": v(5.28, 7.62) * mm, "end": v(5.4, 7.46) * mm});
            skLineSegment(sketch, "E698", {"start": v(5.4, 7.46) * mm, "end": v(5.52, 7.55) * mm});
            skLineSegment(sketch, "E699", {"start": v(5.52, 7.55) * mm, "end": v(5.6, 7.54) * mm});
            skLineSegment(sketch, "E700", {"start": v(5.6, 7.54) * mm, "end": v(5.6, 7.54) * mm});
            skText(sketch, "E701", { "text": "Michigan", "fontName": "OpenSans-Regular.ttf"});
            const initialGuessF2  = {"E701": [-0.01926, -0.00303, 1, 0, 0.00303]};
            skSetInitialGuess(sketch, initialGuessF2);
            skSolve(sketch);
        }
        {
            var Q0;
            Q0 = qSketchRegion(id + "F2", true);
            extrude(context, id + "F3", {"entities" : qUnion([Q0]), "operationType" : NewBodyOperationType.REMOVE, "oppositeDirection" : true, "depth" : 25 * mm, "offsetDistance" : 25 * mm});
        }
    });
